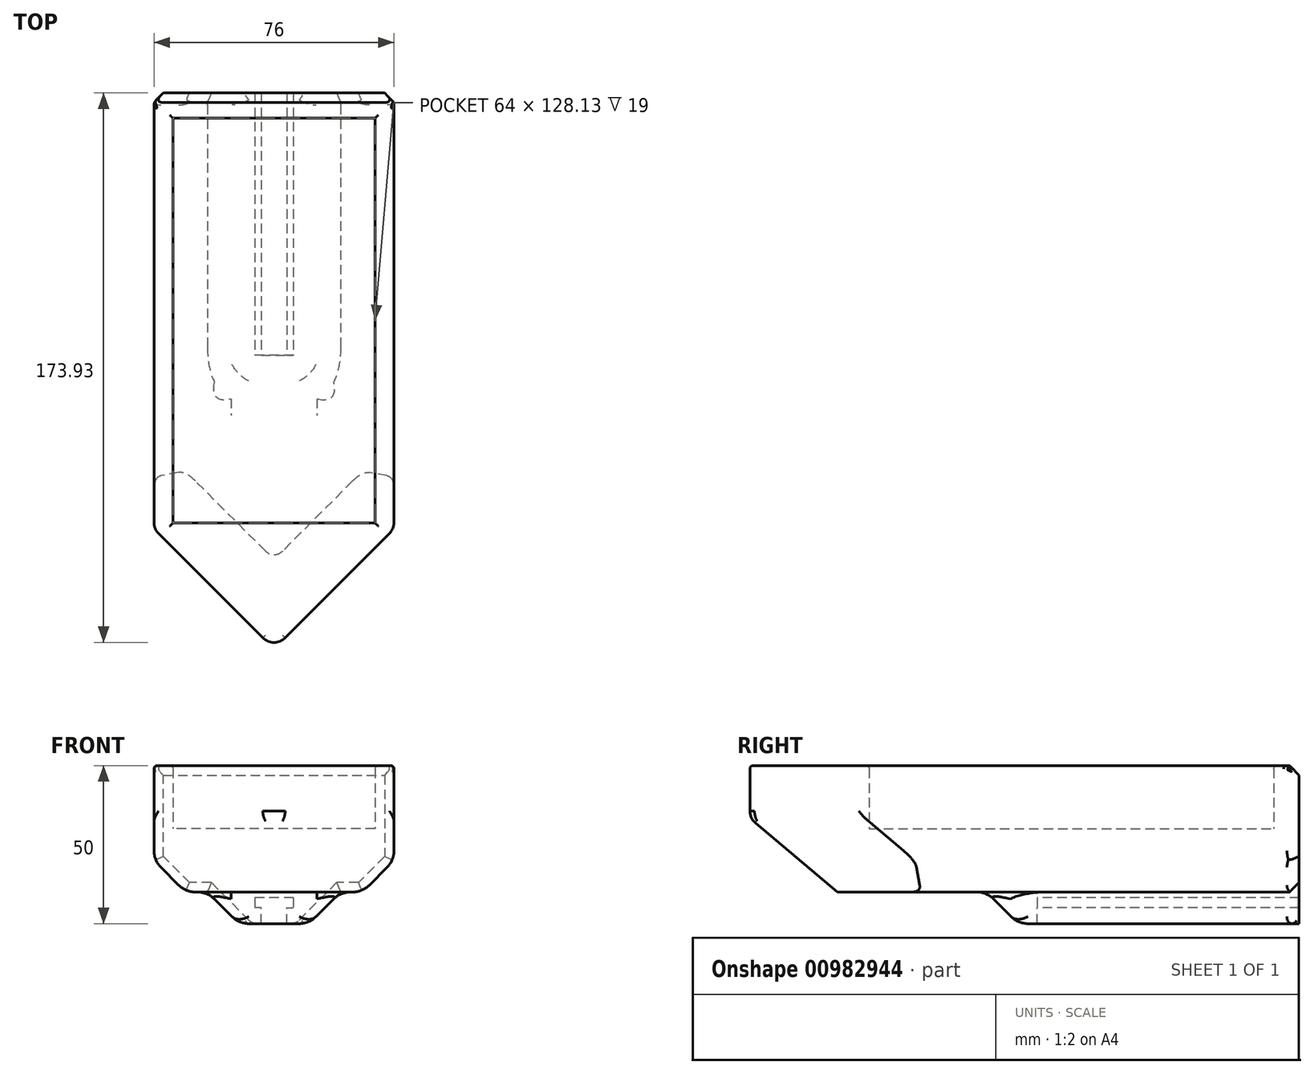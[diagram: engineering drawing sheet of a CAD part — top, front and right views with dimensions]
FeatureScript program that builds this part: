
annotation { "Feature Type Name" : "Feature", "Feature Type Description" : "" }
export const myFeature = defineFeature(function(context is Context, id is Id, definition is map)
    precondition{}
    {
        {
            var Q0;
            Q0=qCreatedBy(makeId("Front.planeOp"),FACE);
            var sketch = newSketch(context, id + "F0", { "sketchPlane" : qUnion([Q0])});
            skLineSegment(sketch, "E0", {"start": v(-6.12, 0) * mm, "end": v(-4.1, 0) * mm});
            skLineSegment(sketch, "E1", {"start": v(-4.1, 0) * mm, "end": v(-4.1, -5) * mm});
            skLineSegment(sketch, "E2", {"start": v(-4.1, -5) * mm, "end": v(-11.1, -5) * mm});
            skLineSegment(sketch, "E3", {"start": v(-11.1, -5) * mm, "end": v(-21.1, 5) * mm});
            skLineSegment(sketch, "E4", {"start": v(-6.12, 0) * mm, "end": v(-6.12, 3.2) * mm});
            skLineSegment(sketch, "E5", {"start": v(-6.12, 3.2) * mm, "end": v(0, 3.2) * mm});
            skLineSegment(sketch, "E6", {"start": v(-21.1, 5) * mm, "end": v(-38, 5) * mm});
            skLineSegment(sketch, "E7", {"start": v(-38, 5) * mm, "end": v(-38, 45) * mm});
            skLineSegment(sketch, "E8", {"start": v(-38, 45) * mm, "end": v(-32, 45) * mm});
            skLineSegment(sketch, "E9", {"start": v(-32, 45) * mm, "end": v(-32, 25) * mm});
            skLineSegment(sketch, "E10", {"start": v(-32, 25) * mm, "end": v(0, 25) * mm});
            skLineSegment(sketch, "E11", {"start": v(-32, 45) * mm, "end": v(0, 45) * mm});
            skLineSegment(sketch, "E12", {"start": v(0, 3.2) * mm, "end": v(0, 45) * mm, "construction": true});
            skLineSegment(sketch, "E13.MirrorCS", {"start": v(6.12, 0) * mm, "end": v(4.1, 0) * mm});
            skLineSegment(sketch, "E14.MirrorCS", {"start": v(6.12, 3.2) * mm, "end": v(0, 3.2) * mm});
            skLineSegment(sketch, "E15.MirrorCS", {"start": v(32, 45) * mm, "end": v(0, 45) * mm});
            skLineSegment(sketch, "E16.MirrorCS", {"start": v(6.12, 0) * mm, "end": v(6.12, 3.2) * mm});
            skLineSegment(sketch, "E17.MirrorCS", {"start": v(32, 25) * mm, "end": v(0, 25) * mm});
            skLineSegment(sketch, "E18.MirrorCS", {"start": v(11.1, -5) * mm, "end": v(21.1, 5) * mm});
            skLineSegment(sketch, "E19.MirrorCS", {"start": v(32, 45) * mm, "end": v(32, 25) * mm});
            skLineSegment(sketch, "E20.MirrorCS", {"start": v(4.1, -5) * mm, "end": v(11.1, -5) * mm});
            skLineSegment(sketch, "E21.MirrorCS", {"start": v(38, 45) * mm, "end": v(32, 45) * mm});
            skLineSegment(sketch, "E22.MirrorCS", {"start": v(4.1, 0) * mm, "end": v(4.1, -5) * mm});
            skLineSegment(sketch, "E23.MirrorCS", {"start": v(38, 5) * mm, "end": v(38, 45) * mm});
            skLineSegment(sketch, "E24.MirrorCS", {"start": v(21.1, 5) * mm, "end": v(38, 5) * mm});
            skLineSegment(sketch, "E25", {"start": v(21.1, 5) * mm, "end": v(-21.1, 5) * mm});
            skLineSegment(sketch, "E26", {"start": v(4.1, -5) * mm, "end": v(-4.1, -5) * mm});
            skSolve(sketch);
        }
        {
            var Q0;
            Q0=makeQuery(id+"F0.imprint","IMPRINT",FACE,{"disambiguationData":[TD([[makeQuery(id+"F0.imprint","IMPRINT",EDGE,{"derivedFrom":sQuery(id+"F0.wireOp",EDGE,"E0")}),-1.0]])]});
            var Q1;
            Q1=makeQuery(id+"F0.imprint","IMPRINT",FACE,{"disambiguationData":[TD([[makeQuery(id+"F0.imprint","IMPRINT",EDGE,{"derivedFrom":sQuery(id+"F0.wireOp",EDGE,"E9")}),1.0]])]});
            var Q2;
            Q2=makeQuery(id+"F0.imprint","IMPRINT",FACE,{"disambiguationData":[TD([[makeQuery(id+"F0.imprint","IMPRINT",EDGE,{"derivedFrom":sQuery(id+"F0.wireOp",EDGE,"E6")}),-1.0]])]});
            extrude(context, id + "F1", {"entities" : qUnion([Q0, Q1, Q2]), "oppositeDirection" : true, "depth" : 8 * mm, "offsetDistance" : 25 * mm});
        }
        {
            var Q0;
            Q0=makeQuery(id+"F0.imprint","IMPRINT",FACE,{"disambiguationData":[TD([[makeQuery(id+"F0.imprint","IMPRINT",EDGE,{"derivedFrom":sQuery(id+"F0.wireOp",EDGE,"E6")}),-1.0]])]});
            extrude(context, id + "F2", {"entities" : qUnion([Q0]), "operationType" : NewBodyOperationType.ADD, "depth" : 130 * mm, "offsetDistance" : 25 * mm});
        }
        {
            var Q0;
            Q0=makeQuery(id+"F0.imprint","IMPRINT",FACE,{"disambiguationData":[TD([[makeQuery(id+"F0.imprint","IMPRINT",EDGE,{"derivedFrom":sQuery(id+"F0.wireOp",EDGE,"E6")}),-1.0]])]});
            var Q1;
            Q1=makeQuery(id+"F0.imprint","IMPRINT",FACE,{"disambiguationData":[TD([[makeQuery(id+"F0.imprint","IMPRINT",EDGE,{"derivedFrom":sQuery(id+"F0.wireOp",EDGE,"E9")}),1.0]])]});
            extrude(context, id + "F3", {"entities" : qUnion([Q0, Q1]), "operationType" : NewBodyOperationType.ADD, "depth" : 170 * mm, "offsetDistance" : 25 * mm, "hasSecondDirection" : true, "secondDirectionOppositeDirection" : false, "secondDirectionDepth" : 128.13 * mm});
        }
        {
            var Q0;
            Q0=makeQuery(id+"F0.imprint","IMPRINT",FACE,{"disambiguationData":[TD([[makeQuery(id+"F0.imprint","IMPRINT",EDGE,{"derivedFrom":sQuery(id+"F0.wireOp",EDGE,"E0")}),-1.0]])]});
            extrude(context, id + "F4", {"entities" : qUnion([Q0]), "operationType" : NewBodyOperationType.ADD, "depth" : 90 * mm, "offsetDistance" : 25 * mm});
        }
        {
            var Q0;
            Q0=makeQuery(id+"F0.imprint","IMPRINT",FACE,{"disambiguationData":[TD([[makeQuery(id+"F0.imprint","IMPRINT",EDGE,{"derivedFrom":sQuery(id+"F0.wireOp",EDGE,"E0")}),-1.0]])]});
            var Q1;
            Q1=makeQuery(id+"F0.imprint","IMPRINT",FACE,{"disambiguationData":[TD([[makeQuery(id+"F0.imprint","IMPRINT",EDGE,{"derivedFrom":sQuery(id+"F0.wireOp",EDGE,"E0")}),1.0]])]});
            extrude(context, id + "F5", {"entities" : qUnion([Q0, Q1]), "operationType" : NewBodyOperationType.ADD, "depth" : 96 * mm, "offsetDistance" : 25 * mm, "hasSecondDirection" : true, "secondDirectionOppositeDirection" : false, "secondDirectionDepth" : 75 * mm});
        }
        {
            var Q0;
            Q0=makeQuery(id+"F5.opExtrude","CAP_EDGE",EDGE,{"disambiguationData":[OSD([sQuery(id+"F0.wireOp",EDGE,"E2"),sQuery(id+"F0.wireOp",EDGE,"E20.MirrorCS"),sQuery(id+"F0.wireOp",EDGE,"E26")])],"isStart":false});
            var Q1;
            {var subQ0=sQuery(id+"F0.wireOp",EDGE,"E25");var subQ1=sQuery(id+"F0.wireOp",EDGE,"E3");var subQ2=sQuery(id+"F0.wireOp",EDGE,"E6");Q1=makeQuery(id+"F11.opFillet","BLEND_EDGE",EDGE,{"blendedFrom":[makeQuery(id+"F5.boolean.opBoolean","MERGE",EDGE,{"derivedFrom":[makeQuery(id+"F4.boolean.opBoolean","MERGE",EDGE,{"derivedFrom":[makeQuery(id+"F1.opExtrude","SWEPT_EDGE",EDGE,{"disambiguationData":[OSD([subQ1,subQ2,subQ0])]}),makeQuery(id+"F4.opExtrude","SWEPT_EDGE",EDGE,{"disambiguationData":[OSD([subQ1,subQ2,subQ0])]})]}),makeQuery(id+"F5.opExtrude","SWEPT_EDGE",EDGE,{"disambiguationData":[OSD([subQ1,subQ2,subQ0])]})]}),makeQuery(id+"F5.opExtrude","CAP_FACE",FACE,{"disambiguationData":[OSD([sQuery(id+"F0.wireOp",EDGE,"E2"),subQ1,sQuery(id+"F0.wireOp",EDGE,"E18.MirrorCS"),sQuery(id+"F0.wireOp",EDGE,"E20.MirrorCS"),subQ0,sQuery(id+"F0.wireOp",EDGE,"E26")])],"isStart":false})],"blendedInto":[makeQuery(id+"F5.opExtrude","CAP_FACE",FACE,{"disambiguationData":[OSD([sQuery(id+"F0.wireOp",EDGE,"E2"),subQ1,sQuery(id+"F0.wireOp",EDGE,"E18.MirrorCS"),sQuery(id+"F0.wireOp",EDGE,"E20.MirrorCS"),subQ0,sQuery(id+"F0.wireOp",EDGE,"E26")])],"isStart":false})]});}
            chamfer(context, id + "F6", {"entities" : qUnion([Q0, Q1]), "width" : 15 * mm, "tangentPropagation" : true});
        }
        {
            var Q0;
            Q0=makeQuery(id+"F3.opExtrude","CAP_EDGE",EDGE,{"disambiguationData":[OSD([sQuery(id+"F0.wireOp",EDGE,"E23.MirrorCS")])],"isStart":false});
            var Q1;
            Q1=makeQuery(id+"F3.opExtrude","CAP_EDGE",EDGE,{"disambiguationData":[OSD([sQuery(id+"F0.wireOp",EDGE,"E7")])],"isStart":false});
            chamfer(context, id + "F7", {"entities" : qUnion([Q0, Q1]), "chamferType" : ChamferType.OFFSET_ANGLE, "width" : 40 * mm, "oppositeDirection" : false, "angle" : 45 * degree, "tangentPropagation" : true});
        }
        {
            var Q0;
            {var subQ0=sQuery(id+"F0.wireOp",EDGE,"E24.MirrorCS");var subQ1=sQuery(id+"F0.wireOp",EDGE,"E6");Q0=makeQuery(id+"F7.opChamfer","BLEND_EDGE",EDGE,{"blendedFrom":[makeQuery(id+"F3.opExtrude","CAP_EDGE",EDGE,{"disambiguationData":[OSD([sQuery(id+"F0.wireOp",EDGE,"E23.MirrorCS")])],"isStart":false}),makeQuery(id+"F3.boolean.opBoolean","MERGE",FACE,{"derivedFrom":[makeQuery(id+"F2.boolean.opBoolean","MERGE",FACE,{"derivedFrom":[makeQuery(id+"F1.opExtrude","SWEPT_FACE",FACE,{"disambiguationData":[OSD([subQ1])]}),makeQuery(id+"F2.opExtrude","SWEPT_FACE",FACE,{"disambiguationData":[OSD([subQ1])]})]}),makeQuery(id+"F2.boolean.opBoolean","MERGE",FACE,{"derivedFrom":[makeQuery(id+"F1.opExtrude","SWEPT_FACE",FACE,{"disambiguationData":[OSD([subQ0])]}),makeQuery(id+"F2.opExtrude","SWEPT_FACE",FACE,{"disambiguationData":[OSD([subQ0])]})]}),makeQuery(id+"F3.opExtrude","SWEPT_FACE",FACE,{"disambiguationData":[OSD([subQ1,subQ0,sQuery(id+"F0.wireOp",EDGE,"E25")])]})]})],"blendedInto":[makeQuery(id+"F3.boolean.opBoolean","MERGE",FACE,{"derivedFrom":[makeQuery(id+"F2.boolean.opBoolean","MERGE",FACE,{"derivedFrom":[makeQuery(id+"F1.opExtrude","SWEPT_FACE",FACE,{"disambiguationData":[OSD([subQ1])]}),makeQuery(id+"F2.opExtrude","SWEPT_FACE",FACE,{"disambiguationData":[OSD([subQ1])]})]}),makeQuery(id+"F2.boolean.opBoolean","MERGE",FACE,{"derivedFrom":[makeQuery(id+"F1.opExtrude","SWEPT_FACE",FACE,{"disambiguationData":[OSD([subQ0])]}),makeQuery(id+"F2.opExtrude","SWEPT_FACE",FACE,{"disambiguationData":[OSD([subQ0])]})]}),makeQuery(id+"F3.opExtrude","SWEPT_FACE",FACE,{"disambiguationData":[OSD([subQ1,subQ0,sQuery(id+"F0.wireOp",EDGE,"E25")])]})]})]});}
            var Q1;
            {var subQ0=sQuery(id+"F0.wireOp",EDGE,"E24.MirrorCS");var subQ1=sQuery(id+"F0.wireOp",EDGE,"E6");Q1=makeQuery(id+"F7.opChamfer","BLEND_EDGE",EDGE,{"blendedFrom":[makeQuery(id+"F3.opExtrude","CAP_EDGE",EDGE,{"disambiguationData":[OSD([sQuery(id+"F0.wireOp",EDGE,"E7")])],"isStart":false}),makeQuery(id+"F3.boolean.opBoolean","MERGE",FACE,{"derivedFrom":[makeQuery(id+"F2.boolean.opBoolean","MERGE",FACE,{"derivedFrom":[makeQuery(id+"F1.opExtrude","SWEPT_FACE",FACE,{"disambiguationData":[OSD([subQ1])]}),makeQuery(id+"F2.opExtrude","SWEPT_FACE",FACE,{"disambiguationData":[OSD([subQ1])]})]}),makeQuery(id+"F2.boolean.opBoolean","MERGE",FACE,{"derivedFrom":[makeQuery(id+"F1.opExtrude","SWEPT_FACE",FACE,{"disambiguationData":[OSD([subQ0])]}),makeQuery(id+"F2.opExtrude","SWEPT_FACE",FACE,{"disambiguationData":[OSD([subQ0])]})]}),makeQuery(id+"F3.opExtrude","SWEPT_FACE",FACE,{"disambiguationData":[OSD([subQ1,subQ0,sQuery(id+"F0.wireOp",EDGE,"E25")])]})]})],"blendedInto":[makeQuery(id+"F3.boolean.opBoolean","MERGE",FACE,{"derivedFrom":[makeQuery(id+"F2.boolean.opBoolean","MERGE",FACE,{"derivedFrom":[makeQuery(id+"F1.opExtrude","SWEPT_FACE",FACE,{"disambiguationData":[OSD([subQ1])]}),makeQuery(id+"F2.opExtrude","SWEPT_FACE",FACE,{"disambiguationData":[OSD([subQ1])]})]}),makeQuery(id+"F2.boolean.opBoolean","MERGE",FACE,{"derivedFrom":[makeQuery(id+"F1.opExtrude","SWEPT_FACE",FACE,{"disambiguationData":[OSD([subQ0])]}),makeQuery(id+"F2.opExtrude","SWEPT_FACE",FACE,{"disambiguationData":[OSD([subQ0])]})]}),makeQuery(id+"F3.opExtrude","SWEPT_FACE",FACE,{"disambiguationData":[OSD([subQ1,subQ0,sQuery(id+"F0.wireOp",EDGE,"E25")])]})]})]});}
            chamfer(context, id + "F8", {"entities" : qUnion([Q0, Q1]), "chamferType" : ChamferType.OFFSET_ANGLE, "width" : 20 * mm, "oppositeDirection" : false, "angle" : 50 * degree, "tangentPropagation" : true});
        }
        {
            var Q0;
            {var subQ0=sQuery(id+"F0.wireOp",EDGE,"E7");var subQ1=sQuery(id+"F0.wireOp",EDGE,"E6");Q0=makeQuery(id+"F3.boolean.opBoolean","MERGE",EDGE,{"derivedFrom":[makeQuery(id+"F2.boolean.opBoolean","MERGE",EDGE,{"derivedFrom":[makeQuery(id+"F1.opExtrude","SWEPT_EDGE",EDGE,{"disambiguationData":[OSD([subQ1,subQ0])]}),makeQuery(id+"F2.opExtrude","SWEPT_EDGE",EDGE,{"disambiguationData":[OSD([subQ1,subQ0])]})]}),makeQuery(id+"F3.opExtrude","SWEPT_EDGE",EDGE,{"disambiguationData":[OSD([subQ1,subQ0])]})]});}
            var Q1;
            {var subQ0=sQuery(id+"F0.wireOp",EDGE,"E24.MirrorCS");var subQ1=sQuery(id+"F0.wireOp",EDGE,"E23.MirrorCS");Q1=makeQuery(id+"F3.boolean.opBoolean","MERGE",EDGE,{"derivedFrom":[makeQuery(id+"F2.boolean.opBoolean","MERGE",EDGE,{"derivedFrom":[makeQuery(id+"F1.opExtrude","SWEPT_EDGE",EDGE,{"disambiguationData":[OSD([subQ1,subQ0])]}),makeQuery(id+"F2.opExtrude","SWEPT_EDGE",EDGE,{"disambiguationData":[OSD([subQ1,subQ0])]})]}),makeQuery(id+"F3.opExtrude","SWEPT_EDGE",EDGE,{"disambiguationData":[OSD([subQ1,subQ0])]})]});}
            chamfer(context, id + "F9", {"entities" : qUnion([Q0, Q1]), "width" : 10 * mm, "tangentPropagation" : true});
        }
        {
            var Q0;
            Q0=makeQuery(id+"F1.opExtrude","CAP_EDGE",EDGE,{"disambiguationData":[OSD([sQuery(id+"F0.wireOp",EDGE,"E8"),sQuery(id+"F0.wireOp",EDGE,"E11"),sQuery(id+"F0.wireOp",EDGE,"E15.MirrorCS"),sQuery(id+"F0.wireOp",EDGE,"E21.MirrorCS")])],"isStart":false});
            var Q1;
            Q1=makeQuery(id+"F1.opExtrude","CAP_EDGE",EDGE,{"disambiguationData":[OSD([sQuery(id+"F0.wireOp",EDGE,"E23.MirrorCS")])],"isStart":false});
            var Q2;
            {var subQ0=sQuery(id+"F0.wireOp",EDGE,"E24.MirrorCS");var subQ1=sQuery(id+"F0.wireOp",EDGE,"E23.MirrorCS");Q2=makeQuery(id+"F9.opChamfer","BLEND_EDGE",EDGE,{"blendedFrom":[makeQuery(id+"F3.boolean.opBoolean","MERGE",EDGE,{"derivedFrom":[makeQuery(id+"F2.boolean.opBoolean","MERGE",EDGE,{"derivedFrom":[makeQuery(id+"F1.opExtrude","SWEPT_EDGE",EDGE,{"disambiguationData":[OSD([subQ1,subQ0])]}),makeQuery(id+"F2.opExtrude","SWEPT_EDGE",EDGE,{"disambiguationData":[OSD([subQ1,subQ0])]})]}),makeQuery(id+"F3.opExtrude","SWEPT_EDGE",EDGE,{"disambiguationData":[OSD([subQ1,subQ0])]})]}),makeQuery(id+"F1.opExtrude","CAP_FACE",FACE,{"disambiguationData":[OSD([sQuery(id+"F0.wireOp",EDGE,"E0"),sQuery(id+"F0.wireOp",EDGE,"E1"),sQuery(id+"F0.wireOp",EDGE,"E2"),sQuery(id+"F0.wireOp",EDGE,"E3"),sQuery(id+"F0.wireOp",EDGE,"E4"),sQuery(id+"F0.wireOp",EDGE,"E5"),sQuery(id+"F0.wireOp",EDGE,"E6"),sQuery(id+"F0.wireOp",EDGE,"E7"),sQuery(id+"F0.wireOp",EDGE,"E8"),sQuery(id+"F0.wireOp",EDGE,"E11"),sQuery(id+"F0.wireOp",EDGE,"E13.MirrorCS"),sQuery(id+"F0.wireOp",EDGE,"E14.MirrorCS"),sQuery(id+"F0.wireOp",EDGE,"E15.MirrorCS"),sQuery(id+"F0.wireOp",EDGE,"E16.MirrorCS"),sQuery(id+"F0.wireOp",EDGE,"E18.MirrorCS"),sQuery(id+"F0.wireOp",EDGE,"E20.MirrorCS"),sQuery(id+"F0.wireOp",EDGE,"E21.MirrorCS"),sQuery(id+"F0.wireOp",EDGE,"E22.MirrorCS"),subQ1,subQ0])],"isStart":false})],"blendedInto":[makeQuery(id+"F1.opExtrude","CAP_FACE",FACE,{"disambiguationData":[OSD([sQuery(id+"F0.wireOp",EDGE,"E0"),sQuery(id+"F0.wireOp",EDGE,"E1"),sQuery(id+"F0.wireOp",EDGE,"E2"),sQuery(id+"F0.wireOp",EDGE,"E3"),sQuery(id+"F0.wireOp",EDGE,"E4"),sQuery(id+"F0.wireOp",EDGE,"E5"),sQuery(id+"F0.wireOp",EDGE,"E6"),sQuery(id+"F0.wireOp",EDGE,"E7"),sQuery(id+"F0.wireOp",EDGE,"E8"),sQuery(id+"F0.wireOp",EDGE,"E11"),sQuery(id+"F0.wireOp",EDGE,"E13.MirrorCS"),sQuery(id+"F0.wireOp",EDGE,"E14.MirrorCS"),sQuery(id+"F0.wireOp",EDGE,"E15.MirrorCS"),sQuery(id+"F0.wireOp",EDGE,"E16.MirrorCS"),sQuery(id+"F0.wireOp",EDGE,"E18.MirrorCS"),sQuery(id+"F0.wireOp",EDGE,"E20.MirrorCS"),sQuery(id+"F0.wireOp",EDGE,"E21.MirrorCS"),sQuery(id+"F0.wireOp",EDGE,"E22.MirrorCS"),subQ1,subQ0])],"isStart":false})]});}
            var Q3;
            Q3=makeQuery(id+"F1.opExtrude","CAP_EDGE",EDGE,{"disambiguationData":[OSD([sQuery(id+"F0.wireOp",EDGE,"E24.MirrorCS")])],"isStart":false});
            var Q4;
            Q4=makeQuery(id+"F1.opExtrude","CAP_EDGE",EDGE,{"disambiguationData":[OSD([sQuery(id+"F0.wireOp",EDGE,"E18.MirrorCS")])],"isStart":false});
            var Q5;
            Q5=makeQuery(id+"F1.opExtrude","CAP_EDGE",EDGE,{"disambiguationData":[OSD([sQuery(id+"F0.wireOp",EDGE,"E3")])],"isStart":false});
            var Q6;
            Q6=makeQuery(id+"F1.opExtrude","CAP_EDGE",EDGE,{"disambiguationData":[OSD([sQuery(id+"F0.wireOp",EDGE,"E6")])],"isStart":false});
            var Q7;
            {var subQ0=sQuery(id+"F0.wireOp",EDGE,"E7");var subQ1=sQuery(id+"F0.wireOp",EDGE,"E6");Q7=makeQuery(id+"F9.opChamfer","BLEND_EDGE",EDGE,{"blendedFrom":[makeQuery(id+"F3.boolean.opBoolean","MERGE",EDGE,{"derivedFrom":[makeQuery(id+"F2.boolean.opBoolean","MERGE",EDGE,{"derivedFrom":[makeQuery(id+"F1.opExtrude","SWEPT_EDGE",EDGE,{"disambiguationData":[OSD([subQ1,subQ0])]}),makeQuery(id+"F2.opExtrude","SWEPT_EDGE",EDGE,{"disambiguationData":[OSD([subQ1,subQ0])]})]}),makeQuery(id+"F3.opExtrude","SWEPT_EDGE",EDGE,{"disambiguationData":[OSD([subQ1,subQ0])]})]}),makeQuery(id+"F1.opExtrude","CAP_FACE",FACE,{"disambiguationData":[OSD([sQuery(id+"F0.wireOp",EDGE,"E0"),sQuery(id+"F0.wireOp",EDGE,"E1"),sQuery(id+"F0.wireOp",EDGE,"E2"),sQuery(id+"F0.wireOp",EDGE,"E3"),sQuery(id+"F0.wireOp",EDGE,"E4"),sQuery(id+"F0.wireOp",EDGE,"E5"),subQ1,subQ0,sQuery(id+"F0.wireOp",EDGE,"E8"),sQuery(id+"F0.wireOp",EDGE,"E11"),sQuery(id+"F0.wireOp",EDGE,"E13.MirrorCS"),sQuery(id+"F0.wireOp",EDGE,"E14.MirrorCS"),sQuery(id+"F0.wireOp",EDGE,"E15.MirrorCS"),sQuery(id+"F0.wireOp",EDGE,"E16.MirrorCS"),sQuery(id+"F0.wireOp",EDGE,"E18.MirrorCS"),sQuery(id+"F0.wireOp",EDGE,"E20.MirrorCS"),sQuery(id+"F0.wireOp",EDGE,"E21.MirrorCS"),sQuery(id+"F0.wireOp",EDGE,"E22.MirrorCS"),sQuery(id+"F0.wireOp",EDGE,"E23.MirrorCS"),sQuery(id+"F0.wireOp",EDGE,"E24.MirrorCS")])],"isStart":false})],"blendedInto":[makeQuery(id+"F1.opExtrude","CAP_FACE",FACE,{"disambiguationData":[OSD([sQuery(id+"F0.wireOp",EDGE,"E0"),sQuery(id+"F0.wireOp",EDGE,"E1"),sQuery(id+"F0.wireOp",EDGE,"E2"),sQuery(id+"F0.wireOp",EDGE,"E3"),sQuery(id+"F0.wireOp",EDGE,"E4"),sQuery(id+"F0.wireOp",EDGE,"E5"),subQ1,subQ0,sQuery(id+"F0.wireOp",EDGE,"E8"),sQuery(id+"F0.wireOp",EDGE,"E11"),sQuery(id+"F0.wireOp",EDGE,"E13.MirrorCS"),sQuery(id+"F0.wireOp",EDGE,"E14.MirrorCS"),sQuery(id+"F0.wireOp",EDGE,"E15.MirrorCS"),sQuery(id+"F0.wireOp",EDGE,"E16.MirrorCS"),sQuery(id+"F0.wireOp",EDGE,"E18.MirrorCS"),sQuery(id+"F0.wireOp",EDGE,"E20.MirrorCS"),sQuery(id+"F0.wireOp",EDGE,"E21.MirrorCS"),sQuery(id+"F0.wireOp",EDGE,"E22.MirrorCS"),sQuery(id+"F0.wireOp",EDGE,"E23.MirrorCS"),sQuery(id+"F0.wireOp",EDGE,"E24.MirrorCS")])],"isStart":false})]});}
            var Q8;
            Q8=makeQuery(id+"F1.opExtrude","CAP_EDGE",EDGE,{"disambiguationData":[OSD([sQuery(id+"F0.wireOp",EDGE,"E7")])],"isStart":false});
            chamfer(context, id + "F10", {"entities" : qUnion([Q0, Q1, Q2, Q3, Q4, Q5, Q6, Q7, Q8]), "width" : 3 * mm, "tangentPropagation" : true});
        }
        {
            var Q0;
            {var subQ0=sQuery(id+"F0.wireOp",EDGE,"E7");var subQ1=sQuery(id+"F0.wireOp",EDGE,"E6");Q0=makeQuery(id+"F9.opChamfer","BLEND_EDGE",EDGE,{"blendedFrom":[makeQuery(id+"F3.boolean.opBoolean","MERGE",EDGE,{"derivedFrom":[makeQuery(id+"F2.boolean.opBoolean","MERGE",EDGE,{"derivedFrom":[makeQuery(id+"F1.opExtrude","SWEPT_EDGE",EDGE,{"disambiguationData":[OSD([subQ1,subQ0])]}),makeQuery(id+"F2.opExtrude","SWEPT_EDGE",EDGE,{"disambiguationData":[OSD([subQ1,subQ0])]})]}),makeQuery(id+"F3.opExtrude","SWEPT_EDGE",EDGE,{"disambiguationData":[OSD([subQ1,subQ0])]})]}),makeQuery(id+"F3.boolean.opBoolean","MERGE",FACE,{"derivedFrom":[makeQuery(id+"F2.boolean.opBoolean","MERGE",FACE,{"derivedFrom":[makeQuery(id+"F1.opExtrude","SWEPT_FACE",FACE,{"disambiguationData":[OSD([subQ0])]}),makeQuery(id+"F2.opExtrude","SWEPT_FACE",FACE,{"disambiguationData":[OSD([subQ0])]})]}),makeQuery(id+"F3.opExtrude","SWEPT_FACE",FACE,{"disambiguationData":[OSD([subQ0])]})]})],"blendedInto":[makeQuery(id+"F3.boolean.opBoolean","MERGE",FACE,{"derivedFrom":[makeQuery(id+"F2.boolean.opBoolean","MERGE",FACE,{"derivedFrom":[makeQuery(id+"F1.opExtrude","SWEPT_FACE",FACE,{"disambiguationData":[OSD([subQ0])]}),makeQuery(id+"F2.opExtrude","SWEPT_FACE",FACE,{"disambiguationData":[OSD([subQ0])]})]}),makeQuery(id+"F3.opExtrude","SWEPT_FACE",FACE,{"disambiguationData":[OSD([subQ0])]})]})]});}
            var Q1;
            {var subQ0=sQuery(id+"F0.wireOp",EDGE,"E25");var subQ1=sQuery(id+"F0.wireOp",EDGE,"E24.MirrorCS");var subQ2=sQuery(id+"F0.wireOp",EDGE,"E6");var subQ3=sQuery(id+"F0.wireOp",EDGE,"E7");Q1=makeQuery(id+"F9.opChamfer","BLEND_EDGE",EDGE,{"blendedFrom":[makeQuery(id+"F3.boolean.opBoolean","MERGE",EDGE,{"derivedFrom":[makeQuery(id+"F2.boolean.opBoolean","MERGE",EDGE,{"derivedFrom":[makeQuery(id+"F1.opExtrude","SWEPT_EDGE",EDGE,{"disambiguationData":[OSD([subQ2,subQ3])]}),makeQuery(id+"F2.opExtrude","SWEPT_EDGE",EDGE,{"disambiguationData":[OSD([subQ2,subQ3])]})]}),makeQuery(id+"F3.opExtrude","SWEPT_EDGE",EDGE,{"disambiguationData":[OSD([subQ2,subQ3])]})]}),makeQuery(id+"F3.boolean.opBoolean","MERGE",FACE,{"derivedFrom":[makeQuery(id+"F2.boolean.opBoolean","MERGE",FACE,{"derivedFrom":[makeQuery(id+"F1.opExtrude","SWEPT_FACE",FACE,{"disambiguationData":[OSD([subQ2])]}),makeQuery(id+"F1.opExtrude","SWEPT_FACE",FACE,{"disambiguationData":[OSD([subQ1])]}),makeQuery(id+"F2.opExtrude","SWEPT_FACE",FACE,{"disambiguationData":[OSD([subQ2,subQ1,subQ0])]})]}),makeQuery(id+"F3.opExtrude","SWEPT_FACE",FACE,{"disambiguationData":[OSD([subQ2,subQ1,subQ0])]})]})],"blendedInto":[makeQuery(id+"F3.boolean.opBoolean","MERGE",FACE,{"derivedFrom":[makeQuery(id+"F2.boolean.opBoolean","MERGE",FACE,{"derivedFrom":[makeQuery(id+"F1.opExtrude","SWEPT_FACE",FACE,{"disambiguationData":[OSD([subQ2])]}),makeQuery(id+"F1.opExtrude","SWEPT_FACE",FACE,{"disambiguationData":[OSD([subQ1])]}),makeQuery(id+"F2.opExtrude","SWEPT_FACE",FACE,{"disambiguationData":[OSD([subQ2,subQ1,subQ0])]})]}),makeQuery(id+"F3.opExtrude","SWEPT_FACE",FACE,{"disambiguationData":[OSD([subQ2,subQ1,subQ0])]})]})]});}
            var Q2;
            {var subQ0=sQuery(id+"F0.wireOp",EDGE,"E25");var subQ1=sQuery(id+"F0.wireOp",EDGE,"E6");var subQ2=sQuery(id+"F0.wireOp",EDGE,"E3");Q2=makeQuery(id+"F4.boolean.opBoolean","MERGE",EDGE,{"derivedFrom":[makeQuery(id+"F1.opExtrude","SWEPT_EDGE",EDGE,{"disambiguationData":[OSD([subQ2,subQ1,subQ0])]}),makeQuery(id+"F4.opExtrude","SWEPT_EDGE",EDGE,{"disambiguationData":[OSD([subQ2,subQ1,subQ0])]})]});}
            var Q3;
            {var subQ0=sQuery(id+"F0.wireOp",EDGE,"E3");var subQ1=sQuery(id+"F0.wireOp",EDGE,"E2");Q3=makeQuery(id+"F4.boolean.opBoolean","MERGE",EDGE,{"derivedFrom":[makeQuery(id+"F1.opExtrude","SWEPT_EDGE",EDGE,{"disambiguationData":[OSD([subQ1,subQ0])]}),makeQuery(id+"F4.opExtrude","SWEPT_EDGE",EDGE,{"disambiguationData":[OSD([subQ1,subQ0])]})]});}
            var Q4;
            {var subQ0=sQuery(id+"F0.wireOp",EDGE,"E20.MirrorCS");var subQ1=sQuery(id+"F0.wireOp",EDGE,"E18.MirrorCS");Q4=makeQuery(id+"F4.boolean.opBoolean","MERGE",EDGE,{"derivedFrom":[makeQuery(id+"F1.opExtrude","SWEPT_EDGE",EDGE,{"disambiguationData":[OSD([subQ1,subQ0])]}),makeQuery(id+"F4.opExtrude","SWEPT_EDGE",EDGE,{"disambiguationData":[OSD([subQ1,subQ0])]})]});}
            var Q5;
            {var subQ0=sQuery(id+"F0.wireOp",EDGE,"E25");var subQ1=sQuery(id+"F0.wireOp",EDGE,"E24.MirrorCS");var subQ2=sQuery(id+"F0.wireOp",EDGE,"E18.MirrorCS");Q5=makeQuery(id+"F4.boolean.opBoolean","MERGE",EDGE,{"derivedFrom":[makeQuery(id+"F1.opExtrude","SWEPT_EDGE",EDGE,{"disambiguationData":[OSD([subQ2,subQ1,subQ0])]}),makeQuery(id+"F4.opExtrude","SWEPT_EDGE",EDGE,{"disambiguationData":[OSD([subQ2,subQ1,subQ0])]})]});}
            var Q6;
            {var subQ0=sQuery(id+"F0.wireOp",EDGE,"E25");var subQ1=sQuery(id+"F0.wireOp",EDGE,"E24.MirrorCS");var subQ2=sQuery(id+"F0.wireOp",EDGE,"E6");var subQ3=sQuery(id+"F0.wireOp",EDGE,"E23.MirrorCS");Q6=makeQuery(id+"F9.opChamfer","BLEND_EDGE",EDGE,{"blendedFrom":[makeQuery(id+"F3.boolean.opBoolean","MERGE",EDGE,{"derivedFrom":[makeQuery(id+"F2.boolean.opBoolean","MERGE",EDGE,{"derivedFrom":[makeQuery(id+"F1.opExtrude","SWEPT_EDGE",EDGE,{"disambiguationData":[OSD([subQ3,subQ1])]}),makeQuery(id+"F2.opExtrude","SWEPT_EDGE",EDGE,{"disambiguationData":[OSD([subQ3,subQ1])]})]}),makeQuery(id+"F3.opExtrude","SWEPT_EDGE",EDGE,{"disambiguationData":[OSD([subQ3,subQ1])]})]}),makeQuery(id+"F3.boolean.opBoolean","MERGE",FACE,{"derivedFrom":[makeQuery(id+"F2.boolean.opBoolean","MERGE",FACE,{"derivedFrom":[makeQuery(id+"F1.opExtrude","SWEPT_FACE",FACE,{"disambiguationData":[OSD([subQ2])]}),makeQuery(id+"F1.opExtrude","SWEPT_FACE",FACE,{"disambiguationData":[OSD([subQ1])]}),makeQuery(id+"F2.opExtrude","SWEPT_FACE",FACE,{"disambiguationData":[OSD([subQ2,subQ1,subQ0])]})]}),makeQuery(id+"F3.opExtrude","SWEPT_FACE",FACE,{"disambiguationData":[OSD([subQ2,subQ1,subQ0])]})]})],"blendedInto":[makeQuery(id+"F3.boolean.opBoolean","MERGE",FACE,{"derivedFrom":[makeQuery(id+"F2.boolean.opBoolean","MERGE",FACE,{"derivedFrom":[makeQuery(id+"F1.opExtrude","SWEPT_FACE",FACE,{"disambiguationData":[OSD([subQ2])]}),makeQuery(id+"F1.opExtrude","SWEPT_FACE",FACE,{"disambiguationData":[OSD([subQ1])]}),makeQuery(id+"F2.opExtrude","SWEPT_FACE",FACE,{"disambiguationData":[OSD([subQ2,subQ1,subQ0])]})]}),makeQuery(id+"F3.opExtrude","SWEPT_FACE",FACE,{"disambiguationData":[OSD([subQ2,subQ1,subQ0])]})]})]});}
            var Q7;
            {var subQ0=sQuery(id+"F0.wireOp",EDGE,"E23.MirrorCS");var subQ1=sQuery(id+"F0.wireOp",EDGE,"E24.MirrorCS");Q7=makeQuery(id+"F9.opChamfer","BLEND_EDGE",EDGE,{"blendedFrom":[makeQuery(id+"F3.boolean.opBoolean","MERGE",EDGE,{"derivedFrom":[makeQuery(id+"F2.boolean.opBoolean","MERGE",EDGE,{"derivedFrom":[makeQuery(id+"F1.opExtrude","SWEPT_EDGE",EDGE,{"disambiguationData":[OSD([subQ0,subQ1])]}),makeQuery(id+"F2.opExtrude","SWEPT_EDGE",EDGE,{"disambiguationData":[OSD([subQ0,subQ1])]})]}),makeQuery(id+"F3.opExtrude","SWEPT_EDGE",EDGE,{"disambiguationData":[OSD([subQ0,subQ1])]})]}),makeQuery(id+"F3.boolean.opBoolean","MERGE",FACE,{"derivedFrom":[makeQuery(id+"F2.boolean.opBoolean","MERGE",FACE,{"derivedFrom":[makeQuery(id+"F1.opExtrude","SWEPT_FACE",FACE,{"disambiguationData":[OSD([subQ0])]}),makeQuery(id+"F2.opExtrude","SWEPT_FACE",FACE,{"disambiguationData":[OSD([subQ0])]})]}),makeQuery(id+"F3.opExtrude","SWEPT_FACE",FACE,{"disambiguationData":[OSD([subQ0])]})]})],"blendedInto":[makeQuery(id+"F3.boolean.opBoolean","MERGE",FACE,{"derivedFrom":[makeQuery(id+"F2.boolean.opBoolean","MERGE",FACE,{"derivedFrom":[makeQuery(id+"F1.opExtrude","SWEPT_FACE",FACE,{"disambiguationData":[OSD([subQ0])]}),makeQuery(id+"F2.opExtrude","SWEPT_FACE",FACE,{"disambiguationData":[OSD([subQ0])]})]}),makeQuery(id+"F3.opExtrude","SWEPT_FACE",FACE,{"disambiguationData":[OSD([subQ0])]})]})]});}
            var Q8;
            Q8=makeQuery(id+"F6.opChamfer","BLEND_FACE",FACE,{"disambiguationData":[OSD([sQuery(id+"F0.wireOp",EDGE,"E2"),sQuery(id+"F0.wireOp",EDGE,"E20.MirrorCS"),sQuery(id+"F0.wireOp",EDGE,"E26")])]});
            fillet(context, id + "F11", {"entities" : qUnion([Q0, Q1, Q2, Q3, Q4, Q5, Q6, Q7, Q8]), "radius" : 7.5 * mm, "tangentPropagation" : true, "allowEdgeOverflow" : false});
        }
        {
            var Q0;
            {var subQ0=sQuery(id+"F0.wireOp",EDGE,"E23.MirrorCS");var subQ1=sQuery(id+"F0.wireOp",EDGE,"E25");var subQ2=sQuery(id+"F0.wireOp",EDGE,"E24.MirrorCS");var subQ3=sQuery(id+"F0.wireOp",EDGE,"E6");Q0=makeQuery(id+"F8.opChamfer","BLEND_EDGE",EDGE,{"blendedFrom":[makeQuery(id+"F7.opChamfer","BLEND_EDGE",EDGE,{"blendedFrom":[makeQuery(id+"F3.opExtrude","CAP_EDGE",EDGE,{"disambiguationData":[OSD([subQ0])],"isStart":false}),makeQuery(id+"F3.boolean.opBoolean","MERGE",FACE,{"derivedFrom":[makeQuery(id+"F2.boolean.opBoolean","MERGE",FACE,{"derivedFrom":[makeQuery(id+"F1.opExtrude","SWEPT_FACE",FACE,{"disambiguationData":[OSD([subQ3])]}),makeQuery(id+"F1.opExtrude","SWEPT_FACE",FACE,{"disambiguationData":[OSD([subQ2])]}),makeQuery(id+"F2.opExtrude","SWEPT_FACE",FACE,{"disambiguationData":[OSD([subQ3,subQ2,subQ1])]})]}),makeQuery(id+"F3.opExtrude","SWEPT_FACE",FACE,{"disambiguationData":[OSD([subQ3,subQ2,subQ1])]})]})],"blendedInto":[makeQuery(id+"F3.boolean.opBoolean","MERGE",FACE,{"derivedFrom":[makeQuery(id+"F2.boolean.opBoolean","MERGE",FACE,{"derivedFrom":[makeQuery(id+"F1.opExtrude","SWEPT_FACE",FACE,{"disambiguationData":[OSD([subQ3])]}),makeQuery(id+"F1.opExtrude","SWEPT_FACE",FACE,{"disambiguationData":[OSD([subQ2])]}),makeQuery(id+"F2.opExtrude","SWEPT_FACE",FACE,{"disambiguationData":[OSD([subQ3,subQ2,subQ1])]})]}),makeQuery(id+"F3.opExtrude","SWEPT_FACE",FACE,{"disambiguationData":[OSD([subQ3,subQ2,subQ1])]})]})]}),makeQuery(id+"F7.opChamfer","BLEND_FACE",FACE,{"disambiguationData":[OSD([subQ0])]})],"blendedInto":[makeQuery(id+"F7.opChamfer","BLEND_FACE",FACE,{"disambiguationData":[OSD([subQ0])]})]});}
            var Q1;
            {var subQ0=sQuery(id+"F0.wireOp",EDGE,"E7");var subQ1=sQuery(id+"F0.wireOp",EDGE,"E25");var subQ2=sQuery(id+"F0.wireOp",EDGE,"E24.MirrorCS");var subQ3=sQuery(id+"F0.wireOp",EDGE,"E6");Q1=makeQuery(id+"F8.opChamfer","BLEND_EDGE",EDGE,{"blendedFrom":[makeQuery(id+"F7.opChamfer","BLEND_EDGE",EDGE,{"blendedFrom":[makeQuery(id+"F3.opExtrude","CAP_EDGE",EDGE,{"disambiguationData":[OSD([subQ0])],"isStart":false}),makeQuery(id+"F3.boolean.opBoolean","MERGE",FACE,{"derivedFrom":[makeQuery(id+"F2.boolean.opBoolean","MERGE",FACE,{"derivedFrom":[makeQuery(id+"F1.opExtrude","SWEPT_FACE",FACE,{"disambiguationData":[OSD([subQ3])]}),makeQuery(id+"F1.opExtrude","SWEPT_FACE",FACE,{"disambiguationData":[OSD([subQ2])]}),makeQuery(id+"F2.opExtrude","SWEPT_FACE",FACE,{"disambiguationData":[OSD([subQ3,subQ2,subQ1])]})]}),makeQuery(id+"F3.opExtrude","SWEPT_FACE",FACE,{"disambiguationData":[OSD([subQ3,subQ2,subQ1])]})]})],"blendedInto":[makeQuery(id+"F3.boolean.opBoolean","MERGE",FACE,{"derivedFrom":[makeQuery(id+"F2.boolean.opBoolean","MERGE",FACE,{"derivedFrom":[makeQuery(id+"F1.opExtrude","SWEPT_FACE",FACE,{"disambiguationData":[OSD([subQ3])]}),makeQuery(id+"F1.opExtrude","SWEPT_FACE",FACE,{"disambiguationData":[OSD([subQ2])]}),makeQuery(id+"F2.opExtrude","SWEPT_FACE",FACE,{"disambiguationData":[OSD([subQ3,subQ2,subQ1])]})]}),makeQuery(id+"F3.opExtrude","SWEPT_FACE",FACE,{"disambiguationData":[OSD([subQ3,subQ2,subQ1])]})]})]}),makeQuery(id+"F7.opChamfer","BLEND_FACE",FACE,{"disambiguationData":[OSD([subQ0])]})],"blendedInto":[makeQuery(id+"F7.opChamfer","BLEND_FACE",FACE,{"disambiguationData":[OSD([subQ0])]})]});}
            var Q2;
            {var subQ0=sQuery(id+"F0.wireOp",EDGE,"E25");var subQ1=sQuery(id+"F0.wireOp",EDGE,"E24.MirrorCS");var subQ2=sQuery(id+"F0.wireOp",EDGE,"E6");var subQ3=makeQuery(id+"F3.boolean.opBoolean","MERGE",FACE,{"derivedFrom":[makeQuery(id+"F2.boolean.opBoolean","MERGE",FACE,{"derivedFrom":[makeQuery(id+"F1.opExtrude","SWEPT_FACE",FACE,{"disambiguationData":[OSD([subQ2])]}),makeQuery(id+"F1.opExtrude","SWEPT_FACE",FACE,{"disambiguationData":[OSD([subQ1])]}),makeQuery(id+"F2.opExtrude","SWEPT_FACE",FACE,{"disambiguationData":[OSD([subQ2,subQ1,subQ0])]})]}),makeQuery(id+"F3.opExtrude","SWEPT_FACE",FACE,{"disambiguationData":[OSD([subQ2,subQ1,subQ0])]})]});Q2=makeQuery(id+"F8.opChamfer","BLEND_EDGE",EDGE,{"blendedFrom":[makeQuery(id+"F7.opChamfer","BLEND_EDGE",EDGE,{"blendedFrom":[makeQuery(id+"F3.opExtrude","CAP_EDGE",EDGE,{"disambiguationData":[OSD([sQuery(id+"F0.wireOp",EDGE,"E7")])],"isStart":false}),subQ3],"blendedInto":[subQ3]}),makeQuery(id+"F7.opChamfer","BLEND_EDGE",EDGE,{"blendedFrom":[makeQuery(id+"F3.opExtrude","CAP_EDGE",EDGE,{"disambiguationData":[OSD([sQuery(id+"F0.wireOp",EDGE,"E23.MirrorCS")])],"isStart":false}),subQ3],"blendedInto":[subQ3]})],"blendedInto":[]});}
            var Q3;
            Q3=makeQuery(id+"F7.opChamfer","BLEND_EDGE",EDGE,{"blendedFrom":[makeQuery(id+"F3.opExtrude","CAP_EDGE",EDGE,{"disambiguationData":[OSD([sQuery(id+"F0.wireOp",EDGE,"E7")])],"isStart":false}),makeQuery(id+"F3.opExtrude","CAP_EDGE",EDGE,{"disambiguationData":[OSD([sQuery(id+"F0.wireOp",EDGE,"E23.MirrorCS")])],"isStart":false})],"blendedInto":[]});
            var Q4;
            {var subQ0=sQuery(id+"F0.wireOp",EDGE,"E23.MirrorCS");Q4=makeQuery(id+"F7.opChamfer","BLEND_EDGE",EDGE,{"blendedFrom":[makeQuery(id+"F3.opExtrude","CAP_EDGE",EDGE,{"disambiguationData":[OSD([subQ0])],"isStart":false}),makeQuery(id+"F3.boolean.opBoolean","MERGE",FACE,{"derivedFrom":[makeQuery(id+"F2.boolean.opBoolean","MERGE",FACE,{"derivedFrom":[makeQuery(id+"F1.opExtrude","SWEPT_FACE",FACE,{"disambiguationData":[OSD([subQ0])]}),makeQuery(id+"F2.opExtrude","SWEPT_FACE",FACE,{"disambiguationData":[OSD([subQ0])]})]}),makeQuery(id+"F3.opExtrude","SWEPT_FACE",FACE,{"disambiguationData":[OSD([subQ0])]})]})],"blendedInto":[makeQuery(id+"F3.boolean.opBoolean","MERGE",FACE,{"derivedFrom":[makeQuery(id+"F2.boolean.opBoolean","MERGE",FACE,{"derivedFrom":[makeQuery(id+"F1.opExtrude","SWEPT_FACE",FACE,{"disambiguationData":[OSD([subQ0])]}),makeQuery(id+"F2.opExtrude","SWEPT_FACE",FACE,{"disambiguationData":[OSD([subQ0])]})]}),makeQuery(id+"F3.opExtrude","SWEPT_FACE",FACE,{"disambiguationData":[OSD([subQ0])]})]})]});}
            var Q5;
            {var subQ0=sQuery(id+"F0.wireOp",EDGE,"E7");Q5=makeQuery(id+"F7.opChamfer","BLEND_EDGE",EDGE,{"blendedFrom":[makeQuery(id+"F3.opExtrude","CAP_EDGE",EDGE,{"disambiguationData":[OSD([subQ0])],"isStart":false}),makeQuery(id+"F3.boolean.opBoolean","MERGE",FACE,{"derivedFrom":[makeQuery(id+"F2.boolean.opBoolean","MERGE",FACE,{"derivedFrom":[makeQuery(id+"F1.opExtrude","SWEPT_FACE",FACE,{"disambiguationData":[OSD([subQ0])]}),makeQuery(id+"F2.opExtrude","SWEPT_FACE",FACE,{"disambiguationData":[OSD([subQ0])]})]}),makeQuery(id+"F3.opExtrude","SWEPT_FACE",FACE,{"disambiguationData":[OSD([subQ0])]})]})],"blendedInto":[makeQuery(id+"F3.boolean.opBoolean","MERGE",FACE,{"derivedFrom":[makeQuery(id+"F2.boolean.opBoolean","MERGE",FACE,{"derivedFrom":[makeQuery(id+"F1.opExtrude","SWEPT_FACE",FACE,{"disambiguationData":[OSD([subQ0])]}),makeQuery(id+"F2.opExtrude","SWEPT_FACE",FACE,{"disambiguationData":[OSD([subQ0])]})]}),makeQuery(id+"F3.opExtrude","SWEPT_FACE",FACE,{"disambiguationData":[OSD([subQ0])]})]})]});}
            fillet(context, id + "F12", {"entities" : qUnion([Q0, Q1, Q2, Q3, Q4, Q5]), "radius" : 5 * mm, "tangentPropagation" : true, "allowEdgeOverflow" : false});
        }
        {
            var Q0;
            Q0=makeQuery(id+"F2.opExtrude","SWEPT_EDGE",EDGE,{"disambiguationData":[OSD([sQuery(id+"F0.wireOp",EDGE,"E15.MirrorCS"),sQuery(id+"F0.wireOp",EDGE,"E19.MirrorCS"),sQuery(id+"F0.wireOp",EDGE,"E21.MirrorCS")])]});
            var Q1;
            {var subQ0=sQuery(id+"F0.wireOp",EDGE,"E23.MirrorCS");var subQ1=sQuery(id+"F0.wireOp",EDGE,"E21.MirrorCS");Q1=makeQuery(id+"F3.boolean.opBoolean","MERGE",EDGE,{"derivedFrom":[makeQuery(id+"F2.boolean.opBoolean","MERGE",EDGE,{"derivedFrom":[makeQuery(id+"F1.opExtrude","SWEPT_EDGE",EDGE,{"disambiguationData":[OSD([subQ1,subQ0])]}),makeQuery(id+"F2.opExtrude","SWEPT_EDGE",EDGE,{"disambiguationData":[OSD([subQ1,subQ0])]})]}),makeQuery(id+"F3.opExtrude","SWEPT_EDGE",EDGE,{"disambiguationData":[OSD([subQ1,subQ0])]})]});}
            var Q2;
            Q2=makeQuery(id+"F2.opExtrude","SWEPT_EDGE",EDGE,{"disambiguationData":[OSD([sQuery(id+"F0.wireOp",EDGE,"E8"),sQuery(id+"F0.wireOp",EDGE,"E9"),sQuery(id+"F0.wireOp",EDGE,"E11")])]});
            var Q3;
            {var subQ0=sQuery(id+"F0.wireOp",EDGE,"E8");var subQ1=sQuery(id+"F0.wireOp",EDGE,"E7");Q3=makeQuery(id+"F3.boolean.opBoolean","MERGE",EDGE,{"derivedFrom":[makeQuery(id+"F2.boolean.opBoolean","MERGE",EDGE,{"derivedFrom":[makeQuery(id+"F1.opExtrude","SWEPT_EDGE",EDGE,{"disambiguationData":[OSD([subQ1,subQ0])]}),makeQuery(id+"F2.opExtrude","SWEPT_EDGE",EDGE,{"disambiguationData":[OSD([subQ1,subQ0])]})]}),makeQuery(id+"F3.opExtrude","SWEPT_EDGE",EDGE,{"disambiguationData":[OSD([subQ1,subQ0])]})]});}
            var Q4;
            Q4=makeQuery(id+"F3.opExtrude","CAP_EDGE",EDGE,{"disambiguationData":[OSD([sQuery(id+"F0.wireOp",EDGE,"E8"),sQuery(id+"F0.wireOp",EDGE,"E11"),sQuery(id+"F0.wireOp",EDGE,"E15.MirrorCS"),sQuery(id+"F0.wireOp",EDGE,"E21.MirrorCS")])],"isStart":true});
            var Q5;
            {var subQ0=sQuery(id+"F0.wireOp",EDGE,"E21.MirrorCS");var subQ1=sQuery(id+"F0.wireOp",EDGE,"E15.MirrorCS");var subQ2=sQuery(id+"F0.wireOp",EDGE,"E11");var subQ3=sQuery(id+"F0.wireOp",EDGE,"E8");Q5=makeQuery(id+"F7.opChamfer","BLEND_EDGE",EDGE,{"blendedFrom":[makeQuery(id+"F3.opExtrude","CAP_EDGE",EDGE,{"disambiguationData":[OSD([sQuery(id+"F0.wireOp",EDGE,"E7")])],"isStart":false}),makeQuery(id+"F3.boolean.opBoolean","MERGE",FACE,{"derivedFrom":[makeQuery(id+"F2.boolean.opBoolean","MERGE",FACE,{"derivedFrom":[makeQuery(id+"F1.opExtrude","SWEPT_FACE",FACE,{"disambiguationData":[OSD([subQ3,subQ2,subQ1,subQ0])]}),makeQuery(id+"F2.opExtrude","SWEPT_FACE",FACE,{"disambiguationData":[OSD([subQ3])]}),makeQuery(id+"F2.opExtrude","SWEPT_FACE",FACE,{"disambiguationData":[OSD([subQ0])]})]}),makeQuery(id+"F3.opExtrude","SWEPT_FACE",FACE,{"disambiguationData":[OSD([subQ3,subQ2,subQ1,subQ0])]})]})],"blendedInto":[makeQuery(id+"F3.boolean.opBoolean","MERGE",FACE,{"derivedFrom":[makeQuery(id+"F2.boolean.opBoolean","MERGE",FACE,{"derivedFrom":[makeQuery(id+"F1.opExtrude","SWEPT_FACE",FACE,{"disambiguationData":[OSD([subQ3,subQ2,subQ1,subQ0])]}),makeQuery(id+"F2.opExtrude","SWEPT_FACE",FACE,{"disambiguationData":[OSD([subQ3])]}),makeQuery(id+"F2.opExtrude","SWEPT_FACE",FACE,{"disambiguationData":[OSD([subQ0])]})]}),makeQuery(id+"F3.opExtrude","SWEPT_FACE",FACE,{"disambiguationData":[OSD([subQ3,subQ2,subQ1,subQ0])]})]})]});}
            var Q6;
            {var subQ0=sQuery(id+"F0.wireOp",EDGE,"E21.MirrorCS");var subQ1=sQuery(id+"F0.wireOp",EDGE,"E15.MirrorCS");var subQ2=sQuery(id+"F0.wireOp",EDGE,"E11");var subQ3=sQuery(id+"F0.wireOp",EDGE,"E8");Q6=makeQuery(id+"F7.opChamfer","BLEND_EDGE",EDGE,{"blendedFrom":[makeQuery(id+"F3.opExtrude","CAP_EDGE",EDGE,{"disambiguationData":[OSD([sQuery(id+"F0.wireOp",EDGE,"E23.MirrorCS")])],"isStart":false}),makeQuery(id+"F3.boolean.opBoolean","MERGE",FACE,{"derivedFrom":[makeQuery(id+"F2.boolean.opBoolean","MERGE",FACE,{"derivedFrom":[makeQuery(id+"F1.opExtrude","SWEPT_FACE",FACE,{"disambiguationData":[OSD([subQ3,subQ2,subQ1,subQ0])]}),makeQuery(id+"F2.opExtrude","SWEPT_FACE",FACE,{"disambiguationData":[OSD([subQ3])]}),makeQuery(id+"F2.opExtrude","SWEPT_FACE",FACE,{"disambiguationData":[OSD([subQ0])]})]}),makeQuery(id+"F3.opExtrude","SWEPT_FACE",FACE,{"disambiguationData":[OSD([subQ3,subQ2,subQ1,subQ0])]})]})],"blendedInto":[makeQuery(id+"F3.boolean.opBoolean","MERGE",FACE,{"derivedFrom":[makeQuery(id+"F2.boolean.opBoolean","MERGE",FACE,{"derivedFrom":[makeQuery(id+"F1.opExtrude","SWEPT_FACE",FACE,{"disambiguationData":[OSD([subQ3,subQ2,subQ1,subQ0])]}),makeQuery(id+"F2.opExtrude","SWEPT_FACE",FACE,{"disambiguationData":[OSD([subQ3])]}),makeQuery(id+"F2.opExtrude","SWEPT_FACE",FACE,{"disambiguationData":[OSD([subQ0])]})]}),makeQuery(id+"F3.opExtrude","SWEPT_FACE",FACE,{"disambiguationData":[OSD([subQ3,subQ2,subQ1,subQ0])]})]})]});}
            var Q7;
            Q7=makeQuery(id+"F1.opExtrude","CAP_EDGE",EDGE,{"disambiguationData":[OSD([sQuery(id+"F0.wireOp",EDGE,"E8"),sQuery(id+"F0.wireOp",EDGE,"E11"),sQuery(id+"F0.wireOp",EDGE,"E15.MirrorCS"),sQuery(id+"F0.wireOp",EDGE,"E21.MirrorCS")])],"isStart":true});
            fillet(context, id + "F13", {"entities" : qUnion([Q0, Q1, Q2, Q3, Q4, Q5, Q6, Q7]), "radius" : 1 * mm, "tangentPropagation" : true, "allowEdgeOverflow" : false});
        }
        {
            var Q0;
            {var subQ0=sQuery(id+"F0.wireOp",EDGE,"E7");Q0=makeQuery(id+"F10.opChamfer","BLEND_EDGE",EDGE,{"blendedFrom":[makeQuery(id+"F1.opExtrude","CAP_EDGE",EDGE,{"disambiguationData":[OSD([subQ0])],"isStart":false}),makeQuery(id+"F3.boolean.opBoolean","MERGE",FACE,{"derivedFrom":[makeQuery(id+"F2.boolean.opBoolean","MERGE",FACE,{"derivedFrom":[makeQuery(id+"F1.opExtrude","SWEPT_FACE",FACE,{"disambiguationData":[OSD([subQ0])]}),makeQuery(id+"F2.opExtrude","SWEPT_FACE",FACE,{"disambiguationData":[OSD([subQ0])]})]}),makeQuery(id+"F3.opExtrude","SWEPT_FACE",FACE,{"disambiguationData":[OSD([subQ0])]})]})],"blendedInto":[makeQuery(id+"F3.boolean.opBoolean","MERGE",FACE,{"derivedFrom":[makeQuery(id+"F2.boolean.opBoolean","MERGE",FACE,{"derivedFrom":[makeQuery(id+"F1.opExtrude","SWEPT_FACE",FACE,{"disambiguationData":[OSD([subQ0])]}),makeQuery(id+"F2.opExtrude","SWEPT_FACE",FACE,{"disambiguationData":[OSD([subQ0])]})]}),makeQuery(id+"F3.opExtrude","SWEPT_FACE",FACE,{"disambiguationData":[OSD([subQ0])]})]})]});}
            var Q1;
            {var subQ0=sQuery(id+"F0.wireOp",EDGE,"E7");var subQ1=sQuery(id+"F0.wireOp",EDGE,"E6");Q1=makeQuery(id+"F10.opChamfer","BLEND_EDGE",EDGE,{"blendedFrom":[makeQuery(id+"F9.opChamfer","BLEND_EDGE",EDGE,{"blendedFrom":[makeQuery(id+"F3.boolean.opBoolean","MERGE",EDGE,{"derivedFrom":[makeQuery(id+"F2.boolean.opBoolean","MERGE",EDGE,{"derivedFrom":[makeQuery(id+"F1.opExtrude","SWEPT_EDGE",EDGE,{"disambiguationData":[OSD([subQ1,subQ0])]}),makeQuery(id+"F2.opExtrude","SWEPT_EDGE",EDGE,{"disambiguationData":[OSD([subQ1,subQ0])]})]}),makeQuery(id+"F3.opExtrude","SWEPT_EDGE",EDGE,{"disambiguationData":[OSD([subQ1,subQ0])]})]}),makeQuery(id+"F1.opExtrude","CAP_FACE",FACE,{"disambiguationData":[OSD([sQuery(id+"F0.wireOp",EDGE,"E0"),sQuery(id+"F0.wireOp",EDGE,"E1"),sQuery(id+"F0.wireOp",EDGE,"E2"),sQuery(id+"F0.wireOp",EDGE,"E3"),sQuery(id+"F0.wireOp",EDGE,"E4"),sQuery(id+"F0.wireOp",EDGE,"E5"),subQ1,subQ0,sQuery(id+"F0.wireOp",EDGE,"E8"),sQuery(id+"F0.wireOp",EDGE,"E11"),sQuery(id+"F0.wireOp",EDGE,"E13.MirrorCS"),sQuery(id+"F0.wireOp",EDGE,"E14.MirrorCS"),sQuery(id+"F0.wireOp",EDGE,"E15.MirrorCS"),sQuery(id+"F0.wireOp",EDGE,"E16.MirrorCS"),sQuery(id+"F0.wireOp",EDGE,"E18.MirrorCS"),sQuery(id+"F0.wireOp",EDGE,"E20.MirrorCS"),sQuery(id+"F0.wireOp",EDGE,"E21.MirrorCS"),sQuery(id+"F0.wireOp",EDGE,"E22.MirrorCS"),sQuery(id+"F0.wireOp",EDGE,"E23.MirrorCS"),sQuery(id+"F0.wireOp",EDGE,"E24.MirrorCS")])],"isStart":false})],"blendedInto":[makeQuery(id+"F1.opExtrude","CAP_FACE",FACE,{"disambiguationData":[OSD([sQuery(id+"F0.wireOp",EDGE,"E0"),sQuery(id+"F0.wireOp",EDGE,"E1"),sQuery(id+"F0.wireOp",EDGE,"E2"),sQuery(id+"F0.wireOp",EDGE,"E3"),sQuery(id+"F0.wireOp",EDGE,"E4"),sQuery(id+"F0.wireOp",EDGE,"E5"),subQ1,subQ0,sQuery(id+"F0.wireOp",EDGE,"E8"),sQuery(id+"F0.wireOp",EDGE,"E11"),sQuery(id+"F0.wireOp",EDGE,"E13.MirrorCS"),sQuery(id+"F0.wireOp",EDGE,"E14.MirrorCS"),sQuery(id+"F0.wireOp",EDGE,"E15.MirrorCS"),sQuery(id+"F0.wireOp",EDGE,"E16.MirrorCS"),sQuery(id+"F0.wireOp",EDGE,"E18.MirrorCS"),sQuery(id+"F0.wireOp",EDGE,"E20.MirrorCS"),sQuery(id+"F0.wireOp",EDGE,"E21.MirrorCS"),sQuery(id+"F0.wireOp",EDGE,"E22.MirrorCS"),sQuery(id+"F0.wireOp",EDGE,"E23.MirrorCS"),sQuery(id+"F0.wireOp",EDGE,"E24.MirrorCS")])],"isStart":false})]}),makeQuery(id+"F9.opChamfer","BLEND_FACE",FACE,{"disambiguationData":[OSD([subQ1,subQ0])]})],"blendedInto":[makeQuery(id+"F9.opChamfer","BLEND_FACE",FACE,{"disambiguationData":[OSD([subQ1,subQ0])]})]});}
            var Q2;
            {var subQ0=sQuery(id+"F0.wireOp",EDGE,"E6");var subQ1=sQuery(id+"F0.wireOp",EDGE,"E25");var subQ2=sQuery(id+"F0.wireOp",EDGE,"E3");Q2=makeQuery(id+"F11.opFillet","BLEND_EDGE",EDGE,{"blendedFrom":[makeQuery(id+"F5.boolean.opBoolean","MERGE",EDGE,{"derivedFrom":[makeQuery(id+"F4.boolean.opBoolean","MERGE",EDGE,{"derivedFrom":[makeQuery(id+"F1.opExtrude","SWEPT_EDGE",EDGE,{"disambiguationData":[OSD([subQ2,subQ0,subQ1])]}),makeQuery(id+"F4.opExtrude","SWEPT_EDGE",EDGE,{"disambiguationData":[OSD([subQ2,subQ0,subQ1])]})]}),makeQuery(id+"F5.opExtrude","SWEPT_EDGE",EDGE,{"disambiguationData":[OSD([subQ2,subQ0,subQ1])]})]}),makeQuery(id+"F10.opChamfer","BLEND_FACE",FACE,{"disambiguationData":[OSD([subQ0])]})],"blendedInto":[makeQuery(id+"F10.opChamfer","BLEND_FACE",FACE,{"disambiguationData":[OSD([subQ0])]})]});}
            var Q3;
            {var subQ0=sQuery(id+"F0.wireOp",EDGE,"E3");Q3=makeQuery(id+"F10.opChamfer","BLEND_EDGE",EDGE,{"blendedFrom":[makeQuery(id+"F1.opExtrude","CAP_EDGE",EDGE,{"disambiguationData":[OSD([subQ0])],"isStart":false}),makeQuery(id+"F5.boolean.opBoolean","MERGE",FACE,{"derivedFrom":[makeQuery(id+"F4.boolean.opBoolean","MERGE",FACE,{"derivedFrom":[makeQuery(id+"F1.opExtrude","SWEPT_FACE",FACE,{"disambiguationData":[OSD([subQ0])]}),makeQuery(id+"F4.opExtrude","SWEPT_FACE",FACE,{"disambiguationData":[OSD([subQ0])]})]}),makeQuery(id+"F5.opExtrude","SWEPT_FACE",FACE,{"disambiguationData":[OSD([subQ0])]})]})],"blendedInto":[makeQuery(id+"F5.boolean.opBoolean","MERGE",FACE,{"derivedFrom":[makeQuery(id+"F4.boolean.opBoolean","MERGE",FACE,{"derivedFrom":[makeQuery(id+"F1.opExtrude","SWEPT_FACE",FACE,{"disambiguationData":[OSD([subQ0])]}),makeQuery(id+"F4.opExtrude","SWEPT_FACE",FACE,{"disambiguationData":[OSD([subQ0])]})]}),makeQuery(id+"F5.opExtrude","SWEPT_FACE",FACE,{"disambiguationData":[OSD([subQ0])]})]})]});}
            var Q4;
            {var subQ0=sQuery(id+"F0.wireOp",EDGE,"E18.MirrorCS");Q4=makeQuery(id+"F10.opChamfer","BLEND_EDGE",EDGE,{"blendedFrom":[makeQuery(id+"F1.opExtrude","CAP_EDGE",EDGE,{"disambiguationData":[OSD([subQ0])],"isStart":false}),makeQuery(id+"F5.boolean.opBoolean","MERGE",FACE,{"derivedFrom":[makeQuery(id+"F4.boolean.opBoolean","MERGE",FACE,{"derivedFrom":[makeQuery(id+"F1.opExtrude","SWEPT_FACE",FACE,{"disambiguationData":[OSD([subQ0])]}),makeQuery(id+"F4.opExtrude","SWEPT_FACE",FACE,{"disambiguationData":[OSD([subQ0])]})]}),makeQuery(id+"F5.opExtrude","SWEPT_FACE",FACE,{"disambiguationData":[OSD([subQ0])]})]})],"blendedInto":[makeQuery(id+"F5.boolean.opBoolean","MERGE",FACE,{"derivedFrom":[makeQuery(id+"F4.boolean.opBoolean","MERGE",FACE,{"derivedFrom":[makeQuery(id+"F1.opExtrude","SWEPT_FACE",FACE,{"disambiguationData":[OSD([subQ0])]}),makeQuery(id+"F4.opExtrude","SWEPT_FACE",FACE,{"disambiguationData":[OSD([subQ0])]})]}),makeQuery(id+"F5.opExtrude","SWEPT_FACE",FACE,{"disambiguationData":[OSD([subQ0])]})]})]});}
            var Q5;
            {var subQ0=sQuery(id+"F0.wireOp",EDGE,"E24.MirrorCS");var subQ1=sQuery(id+"F0.wireOp",EDGE,"E23.MirrorCS");Q5=makeQuery(id+"F10.opChamfer","BLEND_EDGE",EDGE,{"blendedFrom":[makeQuery(id+"F9.opChamfer","BLEND_EDGE",EDGE,{"blendedFrom":[makeQuery(id+"F3.boolean.opBoolean","MERGE",EDGE,{"derivedFrom":[makeQuery(id+"F2.boolean.opBoolean","MERGE",EDGE,{"derivedFrom":[makeQuery(id+"F1.opExtrude","SWEPT_EDGE",EDGE,{"disambiguationData":[OSD([subQ1,subQ0])]}),makeQuery(id+"F2.opExtrude","SWEPT_EDGE",EDGE,{"disambiguationData":[OSD([subQ1,subQ0])]})]}),makeQuery(id+"F3.opExtrude","SWEPT_EDGE",EDGE,{"disambiguationData":[OSD([subQ1,subQ0])]})]}),makeQuery(id+"F1.opExtrude","CAP_FACE",FACE,{"disambiguationData":[OSD([sQuery(id+"F0.wireOp",EDGE,"E0"),sQuery(id+"F0.wireOp",EDGE,"E1"),sQuery(id+"F0.wireOp",EDGE,"E2"),sQuery(id+"F0.wireOp",EDGE,"E3"),sQuery(id+"F0.wireOp",EDGE,"E4"),sQuery(id+"F0.wireOp",EDGE,"E5"),sQuery(id+"F0.wireOp",EDGE,"E6"),sQuery(id+"F0.wireOp",EDGE,"E7"),sQuery(id+"F0.wireOp",EDGE,"E8"),sQuery(id+"F0.wireOp",EDGE,"E11"),sQuery(id+"F0.wireOp",EDGE,"E13.MirrorCS"),sQuery(id+"F0.wireOp",EDGE,"E14.MirrorCS"),sQuery(id+"F0.wireOp",EDGE,"E15.MirrorCS"),sQuery(id+"F0.wireOp",EDGE,"E16.MirrorCS"),sQuery(id+"F0.wireOp",EDGE,"E18.MirrorCS"),sQuery(id+"F0.wireOp",EDGE,"E20.MirrorCS"),sQuery(id+"F0.wireOp",EDGE,"E21.MirrorCS"),sQuery(id+"F0.wireOp",EDGE,"E22.MirrorCS"),subQ1,subQ0])],"isStart":false})],"blendedInto":[makeQuery(id+"F1.opExtrude","CAP_FACE",FACE,{"disambiguationData":[OSD([sQuery(id+"F0.wireOp",EDGE,"E0"),sQuery(id+"F0.wireOp",EDGE,"E1"),sQuery(id+"F0.wireOp",EDGE,"E2"),sQuery(id+"F0.wireOp",EDGE,"E3"),sQuery(id+"F0.wireOp",EDGE,"E4"),sQuery(id+"F0.wireOp",EDGE,"E5"),sQuery(id+"F0.wireOp",EDGE,"E6"),sQuery(id+"F0.wireOp",EDGE,"E7"),sQuery(id+"F0.wireOp",EDGE,"E8"),sQuery(id+"F0.wireOp",EDGE,"E11"),sQuery(id+"F0.wireOp",EDGE,"E13.MirrorCS"),sQuery(id+"F0.wireOp",EDGE,"E14.MirrorCS"),sQuery(id+"F0.wireOp",EDGE,"E15.MirrorCS"),sQuery(id+"F0.wireOp",EDGE,"E16.MirrorCS"),sQuery(id+"F0.wireOp",EDGE,"E18.MirrorCS"),sQuery(id+"F0.wireOp",EDGE,"E20.MirrorCS"),sQuery(id+"F0.wireOp",EDGE,"E21.MirrorCS"),sQuery(id+"F0.wireOp",EDGE,"E22.MirrorCS"),subQ1,subQ0])],"isStart":false})]}),makeQuery(id+"F9.opChamfer","BLEND_FACE",FACE,{"disambiguationData":[OSD([subQ1,subQ0])]})],"blendedInto":[makeQuery(id+"F9.opChamfer","BLEND_FACE",FACE,{"disambiguationData":[OSD([subQ1,subQ0])]})]});}
            var Q6;
            {var subQ0=sQuery(id+"F0.wireOp",EDGE,"E23.MirrorCS");Q6=makeQuery(id+"F10.opChamfer","BLEND_EDGE",EDGE,{"blendedFrom":[makeQuery(id+"F1.opExtrude","CAP_EDGE",EDGE,{"disambiguationData":[OSD([subQ0])],"isStart":false}),makeQuery(id+"F3.boolean.opBoolean","MERGE",FACE,{"derivedFrom":[makeQuery(id+"F2.boolean.opBoolean","MERGE",FACE,{"derivedFrom":[makeQuery(id+"F1.opExtrude","SWEPT_FACE",FACE,{"disambiguationData":[OSD([subQ0])]}),makeQuery(id+"F2.opExtrude","SWEPT_FACE",FACE,{"disambiguationData":[OSD([subQ0])]})]}),makeQuery(id+"F3.opExtrude","SWEPT_FACE",FACE,{"disambiguationData":[OSD([subQ0])]})]})],"blendedInto":[makeQuery(id+"F3.boolean.opBoolean","MERGE",FACE,{"derivedFrom":[makeQuery(id+"F2.boolean.opBoolean","MERGE",FACE,{"derivedFrom":[makeQuery(id+"F1.opExtrude","SWEPT_FACE",FACE,{"disambiguationData":[OSD([subQ0])]}),makeQuery(id+"F2.opExtrude","SWEPT_FACE",FACE,{"disambiguationData":[OSD([subQ0])]})]}),makeQuery(id+"F3.opExtrude","SWEPT_FACE",FACE,{"disambiguationData":[OSD([subQ0])]})]})]});}
            var Q7;
            {var subQ0=sQuery(id+"F0.wireOp",EDGE,"E24.MirrorCS");var subQ1=sQuery(id+"F0.wireOp",EDGE,"E23.MirrorCS");var subQ2=sQuery(id+"F0.wireOp",EDGE,"E22.MirrorCS");var subQ3=sQuery(id+"F0.wireOp",EDGE,"E21.MirrorCS");var subQ4=sQuery(id+"F0.wireOp",EDGE,"E20.MirrorCS");var subQ5=sQuery(id+"F0.wireOp",EDGE,"E18.MirrorCS");var subQ6=sQuery(id+"F0.wireOp",EDGE,"E16.MirrorCS");var subQ7=sQuery(id+"F0.wireOp",EDGE,"E15.MirrorCS");var subQ8=sQuery(id+"F0.wireOp",EDGE,"E14.MirrorCS");var subQ9=sQuery(id+"F0.wireOp",EDGE,"E13.MirrorCS");var subQ10=sQuery(id+"F0.wireOp",EDGE,"E11");var subQ11=sQuery(id+"F0.wireOp",EDGE,"E8");var subQ12=sQuery(id+"F0.wireOp",EDGE,"E7");var subQ13=sQuery(id+"F0.wireOp",EDGE,"E6");var subQ14=sQuery(id+"F0.wireOp",EDGE,"E5");var subQ15=sQuery(id+"F0.wireOp",EDGE,"E4");var subQ16=sQuery(id+"F0.wireOp",EDGE,"E3");var subQ17=sQuery(id+"F0.wireOp",EDGE,"E2");var subQ18=sQuery(id+"F0.wireOp",EDGE,"E1");var subQ19=sQuery(id+"F0.wireOp",EDGE,"E0");var subQ20=makeQuery(id+"F3.boolean.opBoolean","MERGE",EDGE,{"derivedFrom":[makeQuery(id+"F2.boolean.opBoolean","MERGE",EDGE,{"derivedFrom":[makeQuery(id+"F1.opExtrude","SWEPT_EDGE",EDGE,{"disambiguationData":[OSD([subQ1,subQ0])]}),makeQuery(id+"F2.opExtrude","SWEPT_EDGE",EDGE,{"disambiguationData":[OSD([subQ1,subQ0])]})]}),makeQuery(id+"F3.opExtrude","SWEPT_EDGE",EDGE,{"disambiguationData":[OSD([subQ1,subQ0])]})]});Q7=makeQuery(id+"F11.opFillet","BLEND_EDGE",EDGE,{"blendedFrom":[makeQuery(id+"F9.opChamfer","BLEND_EDGE",EDGE,{"blendedFrom":[subQ20,makeQuery(id+"F3.boolean.opBoolean","MERGE",FACE,{"derivedFrom":[makeQuery(id+"F2.boolean.opBoolean","MERGE",FACE,{"derivedFrom":[makeQuery(id+"F1.opExtrude","SWEPT_FACE",FACE,{"disambiguationData":[OSD([subQ1])]}),makeQuery(id+"F2.opExtrude","SWEPT_FACE",FACE,{"disambiguationData":[OSD([subQ1])]})]}),makeQuery(id+"F3.opExtrude","SWEPT_FACE",FACE,{"disambiguationData":[OSD([subQ1])]})]})],"blendedInto":[makeQuery(id+"F3.boolean.opBoolean","MERGE",FACE,{"derivedFrom":[makeQuery(id+"F2.boolean.opBoolean","MERGE",FACE,{"derivedFrom":[makeQuery(id+"F1.opExtrude","SWEPT_FACE",FACE,{"disambiguationData":[OSD([subQ1])]}),makeQuery(id+"F2.opExtrude","SWEPT_FACE",FACE,{"disambiguationData":[OSD([subQ1])]})]}),makeQuery(id+"F3.opExtrude","SWEPT_FACE",FACE,{"disambiguationData":[OSD([subQ1])]})]})]}),makeQuery(id+"F10.opChamfer","BLEND_FACE",FACE,{"disambiguationData":[OSD([subQ19,subQ18,subQ17,subQ16,subQ15,subQ14,subQ13,subQ12,subQ11,subQ10,subQ9,subQ8,subQ7,subQ6,subQ5,subQ4,subQ3,subQ2,subQ1,subQ0]),TDD([makeQuery(id+"F9.opChamfer","BLEND_EDGE",EDGE,{"blendedFrom":[subQ20,makeQuery(id+"F1.opExtrude","CAP_FACE",FACE,{"disambiguationData":[OSD([subQ19,subQ18,subQ17,subQ16,subQ15,subQ14,subQ13,subQ12,subQ11,subQ10,subQ9,subQ8,subQ7,subQ6,subQ5,subQ4,subQ3,subQ2,subQ1,subQ0])],"isStart":false})],"blendedInto":[makeQuery(id+"F1.opExtrude","CAP_FACE",FACE,{"disambiguationData":[OSD([subQ19,subQ18,subQ17,subQ16,subQ15,subQ14,subQ13,subQ12,subQ11,subQ10,subQ9,subQ8,subQ7,subQ6,subQ5,subQ4,subQ3,subQ2,subQ1,subQ0])],"isStart":false})]})])]})],"blendedInto":[makeQuery(id+"F10.opChamfer","BLEND_FACE",FACE,{"disambiguationData":[OSD([subQ19,subQ18,subQ17,subQ16,subQ15,subQ14,subQ13,subQ12,subQ11,subQ10,subQ9,subQ8,subQ7,subQ6,subQ5,subQ4,subQ3,subQ2,subQ1,subQ0]),TDD([makeQuery(id+"F9.opChamfer","BLEND_EDGE",EDGE,{"blendedFrom":[subQ20,makeQuery(id+"F1.opExtrude","CAP_FACE",FACE,{"disambiguationData":[OSD([subQ19,subQ18,subQ17,subQ16,subQ15,subQ14,subQ13,subQ12,subQ11,subQ10,subQ9,subQ8,subQ7,subQ6,subQ5,subQ4,subQ3,subQ2,subQ1,subQ0])],"isStart":false})],"blendedInto":[makeQuery(id+"F1.opExtrude","CAP_FACE",FACE,{"disambiguationData":[OSD([subQ19,subQ18,subQ17,subQ16,subQ15,subQ14,subQ13,subQ12,subQ11,subQ10,subQ9,subQ8,subQ7,subQ6,subQ5,subQ4,subQ3,subQ2,subQ1,subQ0])],"isStart":false})]})])]})]});}
            var Q8;
            {var subQ0=sQuery(id+"F0.wireOp",EDGE,"E23.MirrorCS");var subQ1=sQuery(id+"F0.wireOp",EDGE,"E24.MirrorCS");Q8=makeQuery(id+"F11.opFillet","BLEND_EDGE",EDGE,{"blendedFrom":[makeQuery(id+"F9.opChamfer","BLEND_EDGE",EDGE,{"blendedFrom":[makeQuery(id+"F3.boolean.opBoolean","MERGE",EDGE,{"derivedFrom":[makeQuery(id+"F2.boolean.opBoolean","MERGE",EDGE,{"derivedFrom":[makeQuery(id+"F1.opExtrude","SWEPT_EDGE",EDGE,{"disambiguationData":[OSD([subQ0,subQ1])]}),makeQuery(id+"F2.opExtrude","SWEPT_EDGE",EDGE,{"disambiguationData":[OSD([subQ0,subQ1])]})]}),makeQuery(id+"F3.opExtrude","SWEPT_EDGE",EDGE,{"disambiguationData":[OSD([subQ0,subQ1])]})]}),makeQuery(id+"F3.boolean.opBoolean","MERGE",FACE,{"derivedFrom":[makeQuery(id+"F2.boolean.opBoolean","MERGE",FACE,{"derivedFrom":[makeQuery(id+"F1.opExtrude","SWEPT_FACE",FACE,{"disambiguationData":[OSD([subQ0])]}),makeQuery(id+"F2.opExtrude","SWEPT_FACE",FACE,{"disambiguationData":[OSD([subQ0])]})]}),makeQuery(id+"F3.opExtrude","SWEPT_FACE",FACE,{"disambiguationData":[OSD([subQ0])]})]})],"blendedInto":[makeQuery(id+"F3.boolean.opBoolean","MERGE",FACE,{"derivedFrom":[makeQuery(id+"F2.boolean.opBoolean","MERGE",FACE,{"derivedFrom":[makeQuery(id+"F1.opExtrude","SWEPT_FACE",FACE,{"disambiguationData":[OSD([subQ0])]}),makeQuery(id+"F2.opExtrude","SWEPT_FACE",FACE,{"disambiguationData":[OSD([subQ0])]})]}),makeQuery(id+"F3.opExtrude","SWEPT_FACE",FACE,{"disambiguationData":[OSD([subQ0])]})]})]}),makeQuery(id+"F10.opChamfer","BLEND_FACE",FACE,{"disambiguationData":[OSD([subQ0])]})],"blendedInto":[makeQuery(id+"F10.opChamfer","BLEND_FACE",FACE,{"disambiguationData":[OSD([subQ0])]})]});}
            fillet(context, id + "F14", {"entities" : qUnion([Q0, Q1, Q2, Q3, Q4, Q5, Q6, Q7, Q8]), "radius" : 2 * mm, "tangentPropagation" : true, "allowEdgeOverflow" : false});
        }
    });
